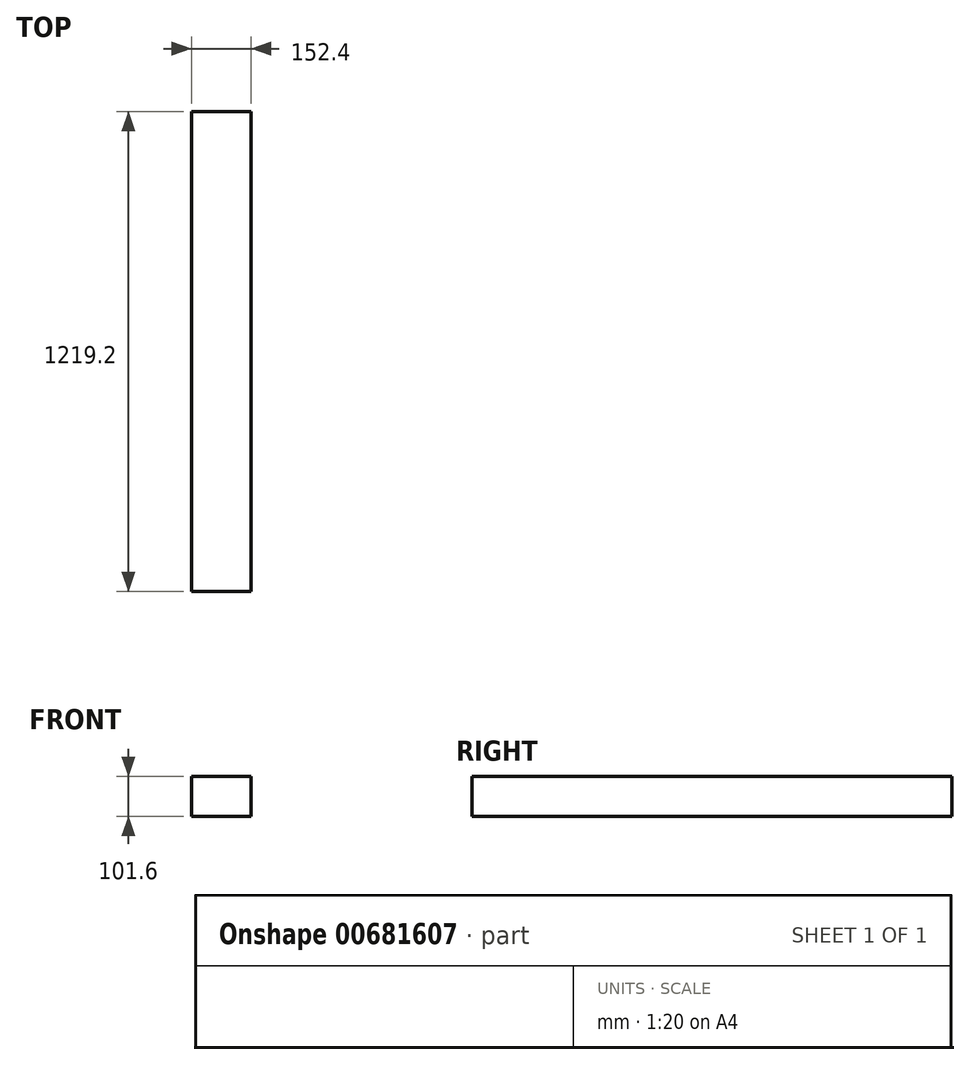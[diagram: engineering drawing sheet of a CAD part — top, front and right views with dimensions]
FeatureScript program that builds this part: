
annotation { "Feature Type Name" : "Feature", "Feature Type Description" : "" }
export const myFeature = defineFeature(function(context is Context, id is Id, definition is map)
    precondition{}
    {
        {
            var Q0;
            Q0=qCreatedBy(makeId("Front.planeOp"),FACE);
            var sketch = newSketch(context, id + "F0", { "sketchPlane" : qUnion([Q0])});
            skLineSegment(sketch, "E0.bottom", {"start": v(76.2, 50.8) * mm, "end": v(-76.2, 50.8) * mm});
            skLineSegment(sketch, "E0.top", {"start": v(76.2, -50.8) * mm, "end": v(-76.2, -50.8) * mm});
            skLineSegment(sketch, "E0.left", {"start": v(76.2, 50.8) * mm, "end": v(76.2, -50.8) * mm});
            skLineSegment(sketch, "E0.right", {"start": v(-76.2, 50.8) * mm, "end": v(-76.2, -50.8) * mm});
            skPoint(sketch, "E0.middle", {"position": v(0, 0) * mm});
            skSolve(sketch);
        }
        {
            var Q0;
            Q0=makeQuery(id+"F0.imprint","IMPRINT",FACE,{"disambiguationData":[TD([[makeQuery(id+"F0.imprint","IMPRINT",EDGE,{"derivedFrom":sQuery(id+"F0.wireOp",EDGE,"E0.bottom")}),1.0]])]});
            extrude(context, id + "F1", {"entities" : qUnion([Q0]), "depth" : 1219.2 * mm, "offsetDistance" : 25.4 * mm});
        }
    });
